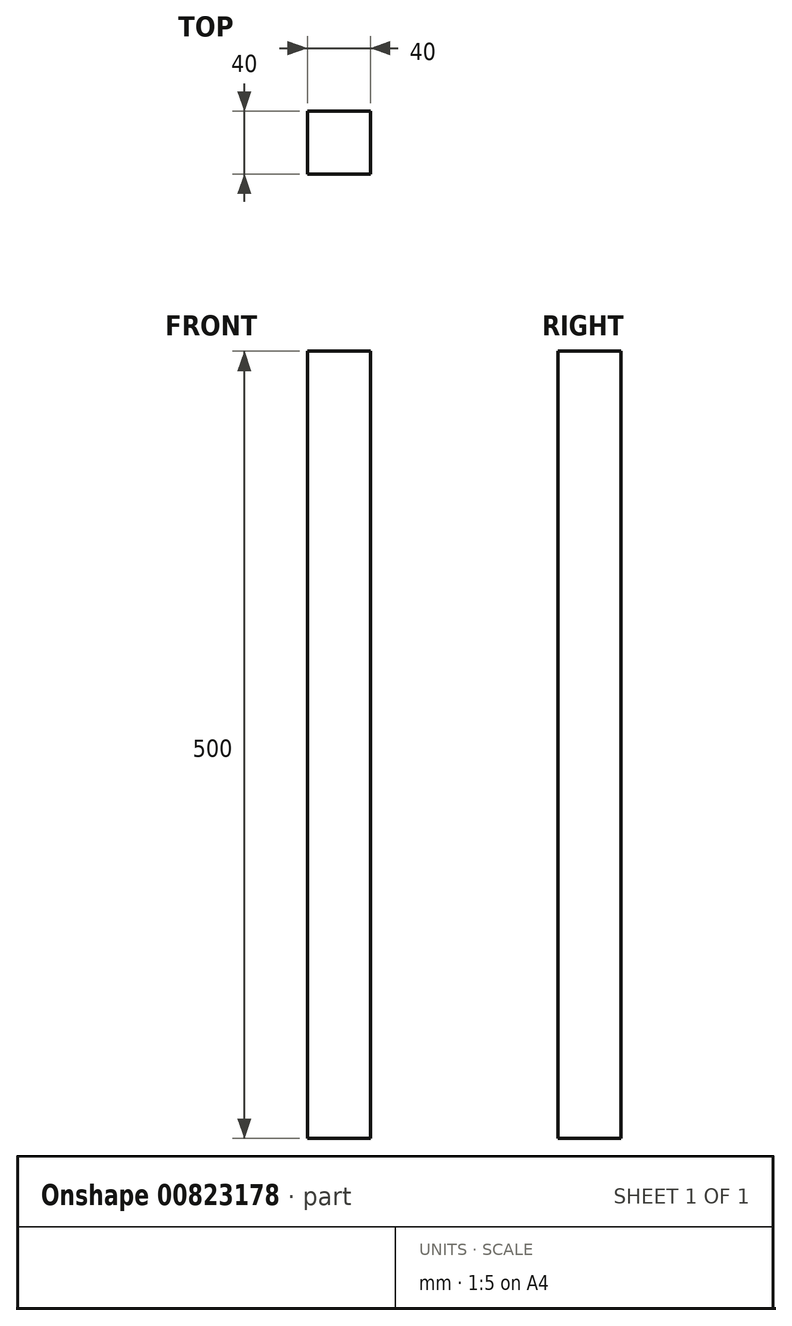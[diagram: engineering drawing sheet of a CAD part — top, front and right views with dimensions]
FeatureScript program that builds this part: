
annotation { "Feature Type Name" : "Feature", "Feature Type Description" : "" }
export const myFeature = defineFeature(function(context is Context, id is Id, definition is map)
    precondition{}
    {
        {
            var Q0;
            Q0=qCreatedBy(makeId("Top.planeOp"),FACE);
            var sketch = newSketch(context, id + "F0", { "sketchPlane" : qUnion([Q0])});
            skLineSegment(sketch, "E0.bottom", {"start": v(-8.35, 10.36) * mm, "end": v(31.65, 10.36) * mm});
            skLineSegment(sketch, "E0.top", {"start": v(-8.35, -29.64) * mm, "end": v(31.65, -29.64) * mm});
            skLineSegment(sketch, "E0.left", {"start": v(-8.35, 10.36) * mm, "end": v(-8.35, -29.64) * mm});
            skLineSegment(sketch, "E0.right", {"start": v(31.65, 10.36) * mm, "end": v(31.65, -29.64) * mm});
            skSolve(sketch);
        }
        {
            var Q0;
            Q0=makeQuery(id+"F0.imprint","IMPRINT",FACE,{"disambiguationData":[TD([[makeQuery(id+"F0.imprint","IMPRINT",EDGE,{"derivedFrom":sQuery(id+"F0.wireOp",EDGE,"E0.bottom")}),-1.0]])]});
            extrude(context, id + "F1", {"entities" : qUnion([Q0]), "depth" : 500 * mm, "offsetDistance" : 25 * mm});
        }
    });
